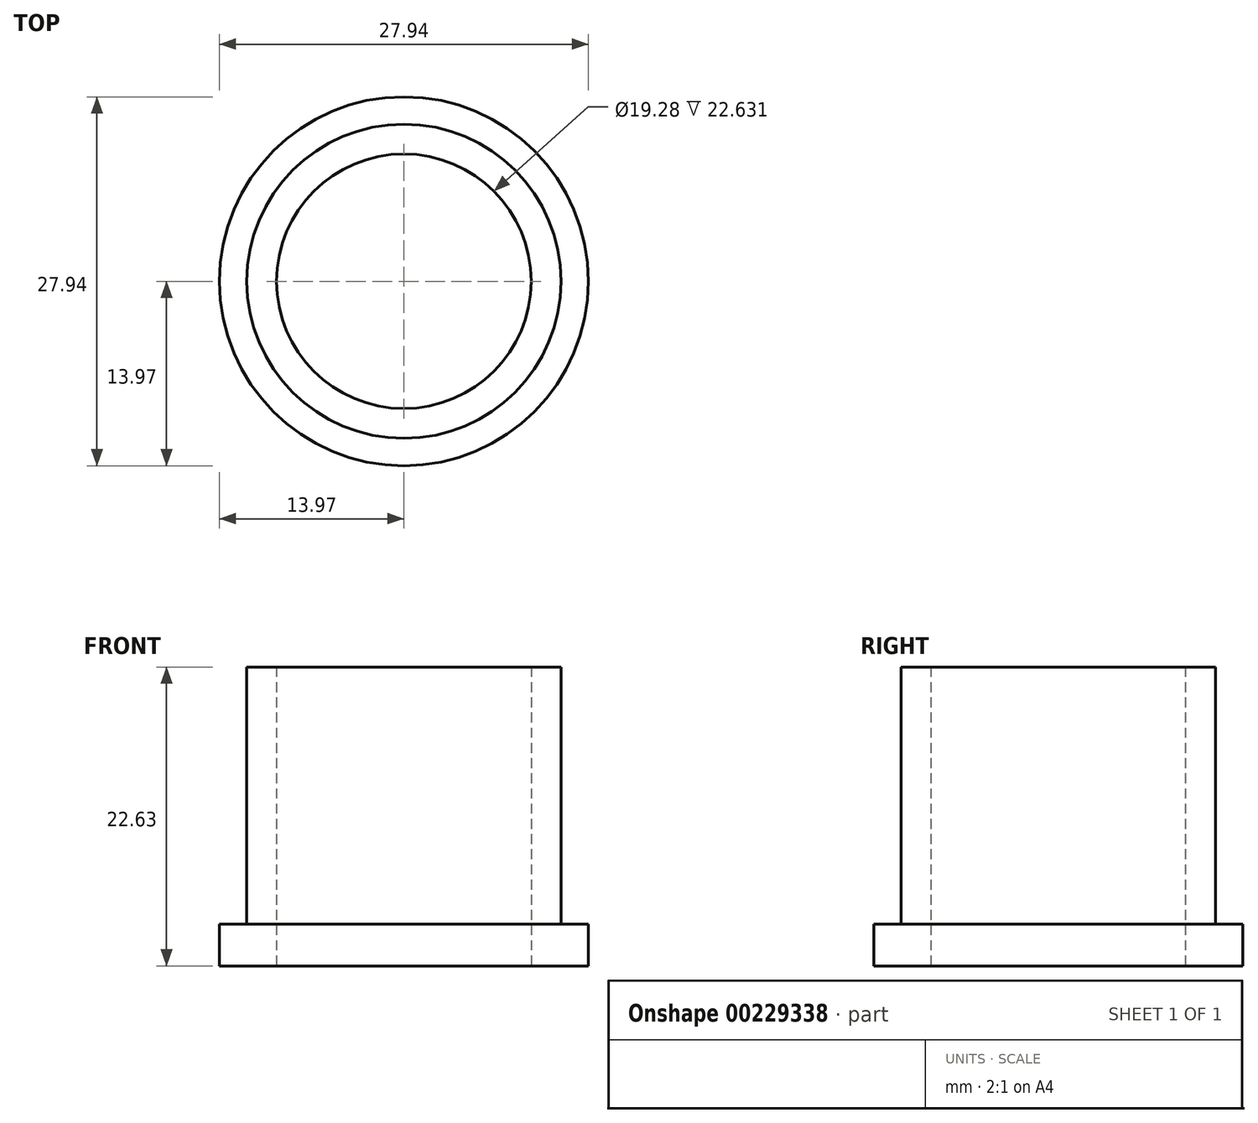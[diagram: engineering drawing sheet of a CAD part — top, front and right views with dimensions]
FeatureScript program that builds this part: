
annotation { "Feature Type Name" : "Feature", "Feature Type Description" : "" }
export const myFeature = defineFeature(function(context is Context, id is Id, definition is map)
    precondition{}
    {
        {
            var Q0;
            Q0=qCreatedBy(makeId("Right.planeOp"),FACE);
            var sketch = newSketch(context, id + "F0", { "sketchPlane" : qUnion([Q0])});
            skLineSegment(sketch, "E0", {"start": v(0, 0) * mm, "end": v(0, 22.63) * mm});
            skLineSegment(sketch, "E1", {"start": v(9.64, 0) * mm, "end": v(9.64, 22.63) * mm});
            skLineSegment(sketch, "E2", {"start": v(13.97, 0) * mm, "end": v(13.97, 3.18) * mm});
            skLineSegment(sketch, "E3", {"start": v(11.9, 3.18) * mm, "end": v(11.9, 22.63) * mm});
            skLineSegment(sketch, "E4", {"start": v(11.9, 3.18) * mm, "end": v(13.97, 3.17) * mm});
            skLineSegment(sketch, "E5", {"start": v(9.64, 0) * mm, "end": v(13.97, 0) * mm});
            skLineSegment(sketch, "E6", {"start": v(11.9, 22.63) * mm, "end": v(9.64, 22.63) * mm});
            skSolve(sketch);
        }
        {
            var Q0;
            Q0=makeQuery(id+"F0.imprint","IMPRINT",FACE,{"disambiguationData":[TD([[makeQuery(id+"F0.imprint","IMPRINT",EDGE,{"derivedFrom":sQuery(id+"F0.wireOp",EDGE,"E1")}),-1.0]])]});
            var Q1;
            Q1=sQuery(id+"F0.wireOp",EDGE,"E0");
            revolve(context, id + "F1", {"entities" : qUnion([Q0]), "axis" : qUnion([Q1]), "revolveType" : RevolveType.FULL});
        }
    });
